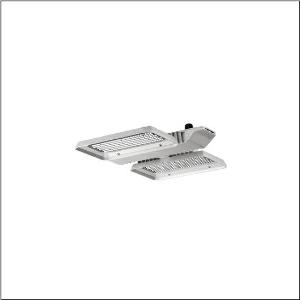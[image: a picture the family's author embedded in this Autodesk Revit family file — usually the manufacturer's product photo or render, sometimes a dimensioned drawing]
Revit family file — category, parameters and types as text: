
# Revit family: highbay_11_51hl62d14dca
name_source: partatom
category: Lighting Fixtures
units: mm (PartAtom-declared; Revit-internal decimal feet)

## family parameters
Cut with Voids When Loaded = No
Host = Face
Light Source = No
Part Type = Normal
Room Calculation Point = No
Round Connector Dimension = Use Diameter
Shared = No

## types (1)
- --- (1 x LED, 10020 lm, 55.6 W, 4000K)
    Apparent Load = 56 VA
    CIE Flux Codes = 89 96 99 100 100
    Color Rendering = 80
    Color Temperature = 4000K
    Default Elevation = 1800 mm
    Description = Highbay 11, LED high bay luminaire, primary light control with lens, of PMMA, light emission: direct distribution, primary light characteristic: symmetric, installation type: surface-mounted, suspended mounting, for 1x 2x LED, rated luminous flux: 10.020lm, luminous efficacy: 180lm/W, light colour: 840, colour temperature: 4000K, control gear: ECG DALI, with terminal, 5-pole, max. 2.5mm², mains connection: 230..240V, AC, 50/60Hz, rated input power: 56W, LED unit, of diecast aluminium, coated, metallic grey (RAL 9006), length: 470mm, width: 500mm, height: 65mm, housing, of diecast aluminium, coated, metallic grey (RAL 9006), protection rating (complete): IP65, insulation class (complete): insulation class I (protective earthing), certification: CE, ENEC, VDE, UKCA, protection symbol: D, impact resistance: IK08 with glass or PC cover, permissible operating ambient temperature: -35..+70°C, corresponds to IFS (International Featured Standards) requirements for safety and quality in the food industry, reducing of maximum allowable ambient temperature of 5°C with ceiling mounting, packaging unit: 1 piece
    Height = 95 mm
    Lamp = 1 x LED
    Lamp Light Flux = 10020 lm
    Lamp Power = 55.6 W
    Lamp count = 1
    Length = 468 mm
    Luminous efficacy = 180 lm/W
    Manufacturer = Siteco
    ModVariant = No
    Model = 51HL62D14DCA
    Mounting Place = Ceiling
    Mounting Type = Pendant
    Number of Poles = 1
    OnlyDefault = Yes
    Power Factor = 1
    Product Name = Highbay 11
    Product group = LED high bay luminaire
    ProductGroupID = 903
    Protection Class = Protection class I
    Protection Degree = IP 65
    RLX_Detail_Level = 1
    RLX_Emergency_Light_Flux = 0 lm
    RLX_Emergency_Type = 0
    RLX_Emergency_Type_DB = No
    RlxData = <blob elided: 70781 chars, md5=526e32a9>
    Socket = socket
    Standby Power = 0 W
    System Light Flux = 10020 lm
    System Power = 56 W
    Type Comments = factory setting: luminous flux: 100 % | dim-lin: 254 | 315 mA
    Type Image = l_1003425.jpg
    URL = http://relux.com
    VarID = @adj_177325
    Voltage = 0 V
    Weight = 0.00 kg
    Width = 501 mm

## geometry (parser evidence)
native form markers: Blend x4, Sweep x10
no freeform markers — native parametric forms only
